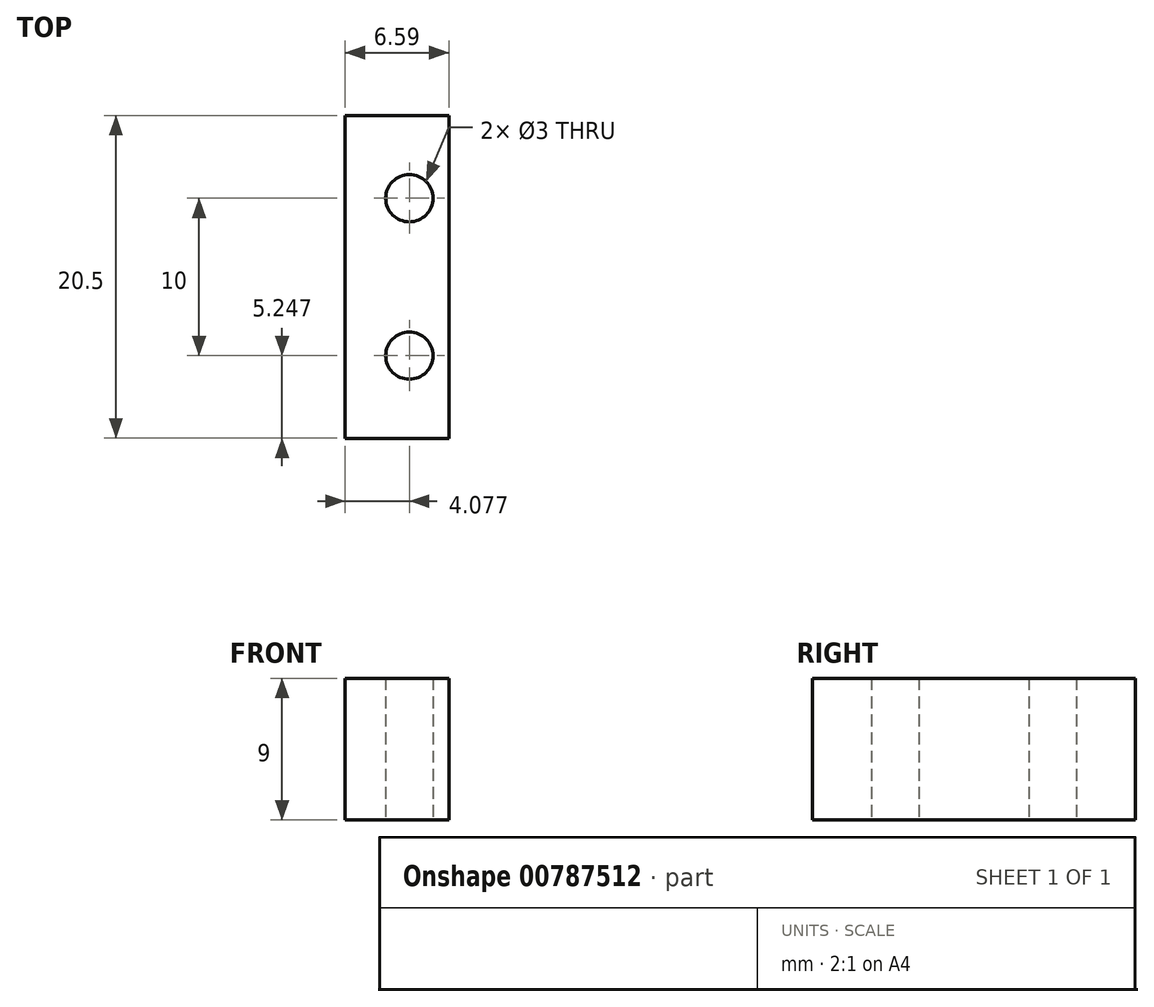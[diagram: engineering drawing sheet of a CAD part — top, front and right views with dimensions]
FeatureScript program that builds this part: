
annotation { "Feature Type Name" : "Feature", "Feature Type Description" : "" }
export const myFeature = defineFeature(function(context is Context, id is Id, definition is map)
    precondition{}
    {
        {
            var Q0;
            Q0=qCreatedBy(makeId("Top.planeOp"),FACE);
            var sketch = newSketch(context, id + "F0", { "sketchPlane" : qUnion([Q0])});
            skCircle(sketch, "E0", {"center": v(-59.95, 20.92) * mm, "radius": 1.5 * mm});
            skCircle(sketch, "E1", {"center": v(-59.95, 10.92) * mm, "radius": 1.5 * mm});
            skLineSegment(sketch, "E2.bottom", {"start": v(-57.44, 26.17) * mm, "end": v(-64.03, 26.17) * mm});
            skLineSegment(sketch, "E2.top", {"start": v(-57.44, 5.67) * mm, "end": v(-64.03, 5.67) * mm});
            skLineSegment(sketch, "E2.left", {"start": v(-57.44, 26.17) * mm, "end": v(-57.44, 5.67) * mm});
            skLineSegment(sketch, "E2.right", {"start": v(-64.03, 26.17) * mm, "end": v(-64.03, 5.67) * mm});
            skSolve(sketch);
        }
        {
            var Q0;
            Q0=makeQuery(id+"F0.imprint","IMPRINT",FACE,{"disambiguationData":[TD([[makeQuery(id+"F0.imprint","IMPRINT",EDGE,{"derivedFrom":sQuery(id+"F0.wireOp",EDGE,"E0")}),-1.0]])]});
            extrude(context, id + "F1", {"entities" : qUnion([Q0]), "depth" : 9 * mm, "offsetDistance" : 25.4 * mm});
        }
    });
